# Revit family: Shower_Bases-Acorn-SBADAR-6438-3F
name_source: partatom
category: Plumbing Fixtures
units: mm (PartAtom-declared; Revit-internal decimal feet)

## family parameters
Cut with Voids When Loaded = No
Host = Face
OmniClass Number = 23.45.05.14.17
OmniClass Title = Showers
Part Type = Normal
Room Calculation Point = No
Round Connector Dimension = Use Diameter
Shared = Yes

## types (1)
- SBADAR-6438-3F
    -VRS Vandal Resistant Strainer = No
    ADA Compliant = Yes
    Assembly Code = D2010710
    Bowl Shape = Rectangular
    CW Connection = No
    CWFU = 1.5
    DIM A = 64"
    DIM B = 38"
    DIM C = 70"
    DIM D = 53 5/8"
    DIM E = 16"
    Default Elevation = 0"
    Description = 64" x 38" ID Terrazzo ADA Shower Base w/ Ramp
    Finish = Precast Terrazzo-Acorn-Terrazzo-Ware
    HW Connection = No
    HWFU = 1.5
    Height = 7 1/2"
    Installation Type = Floor Mounted
    KDG2 Rubber Drain Gasket for 2" Waste Pipe = No
    Length = 53 5/8"
    Manufacturer = Acorn
    Material = Precast Terrazzo-Acorn-Terrazzo-Ware
    Model = SBADAR-6438-3F
    Price = Prices may vary. Please consult Manufacturer Representative for most up-to-date price list.
    Product Documentation Link = https://www.acorneng.com
    Product Page URL = https://www.acorneng.com
    Ramp - Finish = Steel-Acorn-Stainless Steel
    Type Comments = Provide and install an ACORN Shower Base With ADA Compliant Ramp
    URL = https://www.acorneng.com
    Vent Connection = No
    WFU = 3
    Waste Connection = Yes
    Waste Connection Diameter = 2"
    Waste Connection Radius = 1"
    Width = 70"

## geometry (parser evidence)
native form markers: Sweep x2
no freeform markers — native parametric forms only
